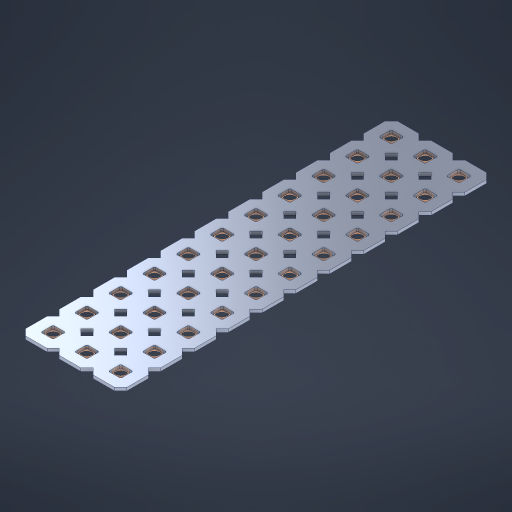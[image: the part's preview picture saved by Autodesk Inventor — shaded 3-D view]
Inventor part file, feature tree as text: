
AUTODESK INVENTOR PART (.ipt)
format: ipt  version: 2023 (Build 270158000, 158)  size: 638,976 bytes
history: native  units: in
note: dims shown in document units (in); Inventor stores cm internally (conversion verified against a paired STEP export)
features: other x34, extrude x32, sketch x2, pattern_linear x1
ambient origin geometry x8: Origin, YZ Plane, XZ Plane, XY Plane, X Axis, Y Axis, Z Axis, Center Point
bodies: Solid1 (feature_tree), Body (feature_tree)
feature tree (69):
  pattern_linear  "Rectangular Pattern1"  Spacing1=0.09in  [1 undecoded]
  sketch  "Sketch1"  dims[d1=0.5in]
  sketch  "Sketch2"  dims[d2=0.182in d3=0.09in d4=0.09in d5=0.09in d6=0.09in d7=0.09in d8=0.09in d9=0.09in d10=0.09in d11=0.02in d13=0.0in d14=0.172in d15=0.0625in d16=0.0in d19=0.5in d22=0.5in]
  other  "Srf1"
  other  "Srf126"
  other  "Srf127"
  other  "Srf128"
  other  "Srf129"
  other  "Srf130"
  other  "Srf131"
  other  "Srf250"
  other  "Srf251"
  other  "Srf252"
  other  "Srf253"
  other  "Srf268"
  other  "Srf269"
  other  "Srf270"
  other  "Srf271"
  other  "Srf272"
  other  "Srf273"
  other  "Srf274"
  other  "Srf275"
  other  "Srf276"
  other  "Srf277"
  other  "Srf278"
  other  "Srf293"
  other  "Srf294"
  other  "Srf295"
  other  "Srf296"
  other  "Srf297"
  other  "Srf298"
  other  "Srf299"
  other  "Srf300"
  other  "Srf301"
  other  "Srf302"
  other  "Srf303"
  other  "Circle"
  extrude  "ExtrusionSrf126"  Depth=0.09in
  extrude  "ExtrusionSrf127"  Depth=0.09in
  extrude  "ExtrusionSrf128"  Depth=0.09in
  extrude  "ExtrusionSrf129"  Depth=0.09in
  extrude  "ExtrusionSrf130"  Depth=0.09in
  extrude  "ExtrusionSrf131"  Depth=0.09in
  extrude  "ExtrusionSrf250"  Depth=0.09in
  extrude  "ExtrusionSrf251"  Depth=0.02in
  extrude  "ExtrusionSrf252"  TaperAngle=0.0deg  [1 undecoded]
  extrude  "ExtrusionSrf253"  Depth=0.5in
  extrude  "ExtrusionSrf268"  Depth=0.5in TaperAngle=0.0deg
  extrude  "ExtrusionSrf269"  Depth=0.5in
  extrude  "ExtrusionSrf270"  Depth=0.5in
  extrude  "ExtrusionSrf271"  [1 undecoded]
  extrude  "ExtrusionSrf272"  [1 undecoded]
  extrude  "ExtrusionSrf273"  [1 undecoded]
  extrude  "ExtrusionSrf274"  [1 undecoded]
  extrude  "ExtrusionSrf275"  [1 undecoded]
  extrude  "ExtrusionSrf276"  [1 undecoded]
  extrude  "ExtrusionSrf277"  [1 undecoded]
  extrude  "ExtrusionSrf278"  [1 undecoded]
  extrude  "ExtrusionSrf293"  [1 undecoded]
  extrude  "ExtrusionSrf294"  [1 undecoded]
  extrude  "ExtrusionSrf295"  [1 undecoded]
  extrude  "ExtrusionSrf296"  [1 undecoded]
  extrude  "ExtrusionSrf297"  [1 undecoded]
  extrude  "ExtrusionSrf298"  [1 undecoded]
  extrude  "ExtrusionSrf299"  [1 undecoded]
  extrude  "ExtrusionSrf300"  [1 undecoded]
  extrude  "ExtrusionSrf301"  [1 undecoded]
  extrude  "ExtrusionSrf302"  [1 undecoded]
  extrude  "ExtrusionSrf303"  [1 undecoded]
note: 21 required parameter values undecoded (feature->parameter linkage not recoverable at this tier; creation-order binding heuristic only, values carry confidence <= 0.55)
